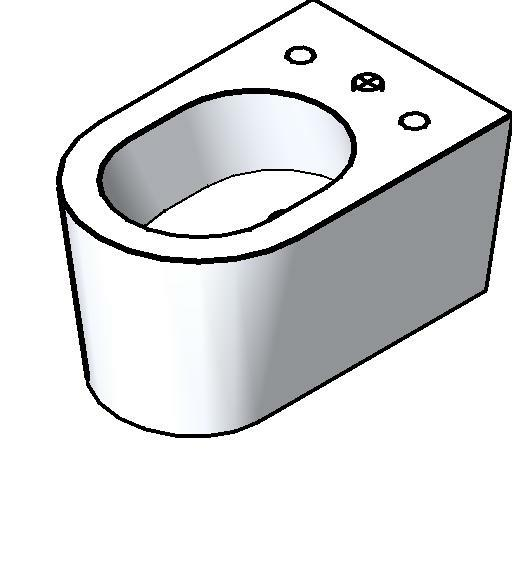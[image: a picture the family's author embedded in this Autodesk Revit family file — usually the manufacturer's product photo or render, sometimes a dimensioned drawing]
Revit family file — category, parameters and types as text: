
# Revit family: Deca_Bide 3 furos suspenso_LK_B.232
name_source: partatom
category: Plumbing Fixtures
units: mm (PartAtom-declared; Revit-internal decimal feet)

## family parameters
Cut with Voids When Loaded = No
Host = Face
Part Type = Normal
Room Calculation Point = No
Round Connector Dimension = Use Radius
Shared = No

## types (1)
- B.232.17_Branco
    Acompanha o Produto = -
    Aprovado por = quattroD
    Atendimento ao Cliente = 0800-0117073
    CWFU = 0
    Categoria = BACIAS E BIDES
    Composição Anel Vedação = -
    Composição Assento = -
    Composição Básica = Argila, feldspato, caulim, vidrados e corantes inorgânicos.
    Composição Componente = Não Possui
    Consumo = -
    Cor Interna = -
    Cor Principal = Branco
    Cor Secundária = -
    Cores Componente = Não Possui
    Criado por = quattroD
    Código Pai = B.232
    Default Elevation = 0 mm  [stored 0 ft]
    Description = Bidê suspenso com 3 furos
    Diâmetro Ponto de Esgoto = 40 mm  [stored 0.131234 ft]
    Diâmetro Água Fria = 15 mm  [stored 0.0492126 ft]
    Diâmetro Água Quente = 15 mm  [stored 0.0492126 ft]
    Informações Complementares = -
    Itens de Instalação = 1895.C14; 1895.C26; 1895.C33; 1895.C34; 1895.C35; 1895.C37; 1895.C38; 1895.C40.CR; 1895.C43; 1895.C50; 1895.C52; 1895.C64; 1895.C81; 1895.C84; 1895.C86; 1895.C87; 1895.C90; 1895.C94; SP.132.01
    Linha = LK
    Manufacturer = Deca
    Material = Deca_Branco
    Model = B.232.17
    Norma = NBR-16728-1;NBR-16728-2
    Peso Líquido (Kg) = 26.218
    Pressão máx. funcionamento = -
    Pressão mín. Aquec. Acúmulo = -
    Pressão mín. Aquec. Passagem = -
    Pressão mín. funcionamento = -
    Raio Ponto de Esgoto = 20 mm  [stored 0.0656168 ft]
    Raio Água Fria = 8 mm  [stored 0.0262467 ft]
    Raio Água Quente = 8 mm  [stored 0.0262467 ft]
    Saída de Esgoto = Saída de Esgoto Horizontal
    Segmento = Banheiro Luxo
    Tipo de dispositivo economizador = -
    Tipo de mecanismo utilizado = -
    Tipo de rosca de entrada = -
    Tipo de rosca de saída = -
    URL = www.deca.com.br
    Vazão na Pressão máx. (L/min) = -
    Vazão na Pressão mín. (L/min) = -
    WFU = 0

note: [stored X ft] marks values corroborated as IEEE doubles in the binary element streams (Revit-internal decimal feet)

## geometry (parser evidence)
native form markers: Sweep x2
no freeform markers — native parametric forms only
